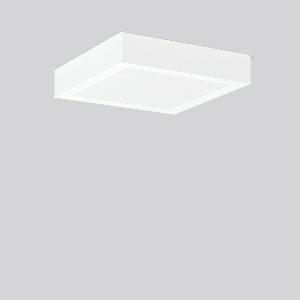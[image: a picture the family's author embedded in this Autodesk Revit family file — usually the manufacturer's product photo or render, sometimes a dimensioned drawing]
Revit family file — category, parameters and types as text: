
# Revit family: toledo_flat_square_a_672277_002_04_e70c
name_source: partatom
category: Lighting Fixtures
units: mm (PartAtom-declared; Revit-internal decimal feet)

## family parameters
Cut with Voids When Loaded = No
Host = Face
Light Source = No
Part Type = Normal
Room Calculation Point = No
Round Connector Dimension = Use Diameter
Shared = No

## types (1)
- TOLEDO FLAT square A (1 x LED Modul 830, 2050 lm, 3000)
    Apparent Load = 25 VA
    CIE Flux Codes = 48 80 96 100 100
    Color Rendering = 80
    Color Temperature = 3000
    Default Elevation = 1800 mm
    Description = Series: TOLEDO FLAT square
Ultra thin surface mounted downlight. For escape route illumination. Surface mounted housing: sheet steel, powder-coated. Square cover plate: die-cast aluminium, powder coated. Light guide and diffuser made of non-yellowing PMMA, opal matt. Self-contained system with automatic self-test and feedback to the RZB monitoring system MULTIDIGIT. 
Colour: white
Length: 300 mm
Width: 300 mm
Height: 58 mm
Weight: 3.96 kg
Operating mode: maintained power mode
Duration time: 3 h
Lamp: LED
Socket: without socket
Colour temperature: 3000K
Colour rendering index (CRI): 80
System power: 25 W
Rated luminous flux: 2050 lm
Luminous flux, emergency: 420 lm
System power, emergency: -
Control gear: Regulated power supply
Protection class: I
Type of protection: IP 40
    Height = 58 mm
    Lamp = 1 x LED Modul 830
    Lamp Light Flux = 2050 lm
    Lamp count = 1
    Length = 300 mm
    Lifetime = 50000 h
    Luminous efficacy = 82 lm/W
    Manufacturer = RZB
    ModVariant = No
    Model = 672277.002.04
    Mounting Place = Ceiling
    Mounting Type = Surface mounted
    Number of Poles = 1
    OnlyDefault = Yes
    Power Factor = 1
    Product Name = TOLEDO FLAT square A
    Product group = Surface mounted downlights
    ProductGroupID = 302
    Protection Class = Protection class I
    Protection Degree = IP 40
    RLX_Detail_Level = 1
    RLX_Emergency_Light_Flux = 420 lm
    RLX_Emergency_Type = 3
    RLX_Emergency_Type_DB = Yes
    RlxData = <blob elided: 14053 chars, md5=66eba598>
    Socket = socket
    Standby Power = 0 W
    System Light Flux = 2050 lm
    System Power = 25 W
    Type Comments = Product without accessories
    Type Image = 901554.002.jpg
    URL = http://relux.com
    VarID = ---
    Voltage = 0 V
    Weight = 0.00 kg
    Width = 300 mm

## geometry (parser evidence)
native form markers: Sweep x12
no freeform markers — native parametric forms only
